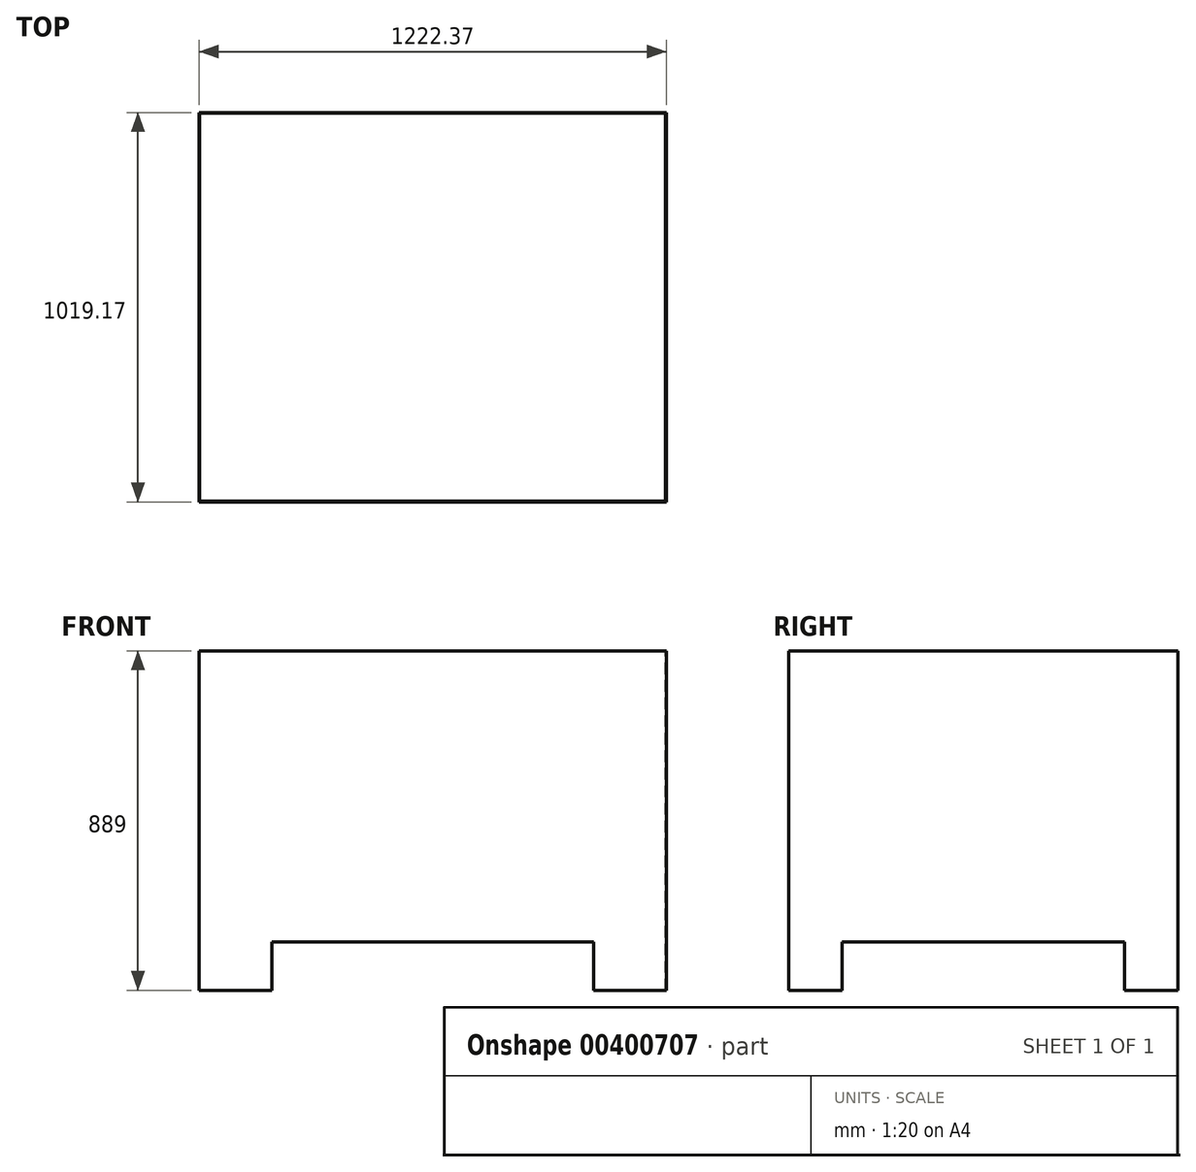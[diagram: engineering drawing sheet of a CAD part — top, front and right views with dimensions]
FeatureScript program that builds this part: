
annotation { "Feature Type Name" : "Feature", "Feature Type Description" : "" }
export const myFeature = defineFeature(function(context is Context, id is Id, definition is map)
    precondition{}
    {
        {
            var Q0;
            Q0=qCreatedBy(makeId("Front.planeOp"),FACE);
            var sketch = newSketch(context, id + "F0", { "sketchPlane" : qUnion([Q0])});
            skLineSegment(sketch, "E0.bottom", {"start": v(0, 0) * mm, "end": v(481.25, 0) * mm});
            skLineSegment(sketch, "E0.top", {"start": v(0, 350) * mm, "end": v(481.25, 350) * mm});
            skLineSegment(sketch, "E0.left", {"start": v(0, 0) * mm, "end": v(0, 350) * mm});
            skLineSegment(sketch, "E0.right", {"start": v(481.25, 0) * mm, "end": v(481.25, 350) * mm});
            skSolve(sketch);
        }
        {
            var Q0;
            Q0 = qSketchRegion(id + "F0", true);
            extrude(context, id + "F1", {"entities" : qUnion([Q0]), "oppositeDirection" : true, "depth" : 401.25 * mm});
        }
        {
            var Q0;
            Q0=makeQuery(id+"F1.opExtrude","SWEPT_FACE",FACE,{"disambiguationData":[OSD([sQuery(id+"F0.wireOp",EDGE,"E0.top")])]});
            var sketch = newSketch(context, id + "F2", { "sketchPlane" : qUnion([Q0])});
            skLineSegment(sketch, "E1.bottom", {"start": v(480.62, 0.63) * mm, "end": v(0.62, 0.63) * mm});
            skLineSegment(sketch, "E1.top", {"start": v(480.62, 400.63) * mm, "end": v(0.62, 400.63) * mm});
            skLineSegment(sketch, "E1.left", {"start": v(480.62, 0.63) * mm, "end": v(480.62, 400.63) * mm});
            skLineSegment(sketch, "E1.right", {"start": v(0.62, 0.63) * mm, "end": v(0.62, 400.63) * mm});
            skPoint(sketch, "E1.middle", {"position": v(240.62, 200.63) * mm});
            skPoint(sketch, "E1.middle.positionSnap0", {"position": v(0, 200.63) * mm});
            skPoint(sketch, "E1.middle.positionSnap1", {"position": v(240.62, 401.25) * mm});
            skPoint(sketch, "E1.centerSnap0", {"position": v(0, 200.63) * mm});
            skPoint(sketch, "E1.centerSnap1", {"position": v(240.62, 401.25) * mm});
            skSolve(sketch);
        }
        {
            var Q0;
            Q0 = qSketchRegion(id + "F2", true);
            extrude(context, id + "F3", {"entities" : qUnion([Q0]), "operationType" : NewBodyOperationType.REMOVE, "endBound" : BoundingType.THROUGH_ALL, "oppositeDirection" : true, "depth" : 25 * mm});
        }
        {
            var Q0;
            Q0=makeQuery(id+"F1.opExtrude","SWEPT_FACE",FACE,{"disambiguationData":[OSD([sQuery(id+"F0.wireOp",EDGE,"E0.left")])]});
            var sketch = newSketch(context, id + "F4", { "sketchPlane" : qUnion([Q0])});
            skLineSegment(sketch, "E2", {"start": v(-401.25, 0) * mm, "end": v(-346.25, 0) * mm});
            skLineSegment(sketch, "E3", {"start": v(-346.25, 0) * mm, "end": v(-346.25, 50) * mm});
            skLineSegment(sketch, "E4.bottom", {"start": v(-346.25, 50) * mm, "end": v(-55, 50) * mm});
            skLineSegment(sketch, "E4.top", {"start": v(-346.25, -50) * mm, "end": v(-55, -50) * mm});
            skLineSegment(sketch, "E4.left", {"start": v(-346.25, 50) * mm, "end": v(-346.25, -50) * mm});
            skLineSegment(sketch, "E4.right", {"start": v(-55, 50) * mm, "end": v(-55, -50) * mm});
            skPoint(sketch, "E4.middle", {"position": v(-200.63, 0) * mm});
            skSolve(sketch);
        }
        {
            var Q0;
            Q0 = qSketchRegion(id + "F4", true);
            extrude(context, id + "F5", {"entities" : qUnion([Q0]), "operationType" : NewBodyOperationType.REMOVE, "endBound" : BoundingType.THROUGH_ALL, "oppositeDirection" : true, "depth" : 25 * mm});
        }
        {
            var Q0;
            Q0=makeQuery(id+"F1.opExtrude","CAP_FACE",FACE,{"disambiguationData":[OSD([sQuery(id+"F0.wireOp",EDGE,"E0.bottom"),sQuery(id+"F0.wireOp",EDGE,"E0.top"),sQuery(id+"F0.wireOp",EDGE,"E0.left"),sQuery(id+"F0.wireOp",EDGE,"E0.right")])],"isStart":true});
            var sketch = newSketch(context, id + "F6", { "sketchPlane" : qUnion([Q0])});
            skLineSegment(sketch, "E5", {"start": v(0, 0) * mm, "end": v(75, 0) * mm});
            skLineSegment(sketch, "E6", {"start": v(75, 0) * mm, "end": v(75, 50) * mm});
            skLineSegment(sketch, "E7.bottom", {"start": v(75, 50) * mm, "end": v(406.25, 50) * mm});
            skLineSegment(sketch, "E7.top", {"start": v(75, -50) * mm, "end": v(406.25, -50) * mm});
            skLineSegment(sketch, "E7.left", {"start": v(75, 50) * mm, "end": v(75, -50) * mm});
            skLineSegment(sketch, "E7.right", {"start": v(406.25, 50) * mm, "end": v(406.25, -50) * mm});
            skPoint(sketch, "E7.middle", {"position": v(240.62, 0) * mm});
            skSolve(sketch);
        }
        {
            var Q0;
            Q0 = qSketchRegion(id + "F6", true);
            extrude(context, id + "F7", {"entities" : qUnion([Q0]), "operationType" : NewBodyOperationType.REMOVE, "endBound" : BoundingType.THROUGH_ALL, "oppositeDirection" : true, "depth" : 25 * mm});
        }
        {
            var Q0;
            Q0=makeQuery(id+"F1.opExtrude","SWEPT_BODY",BODY,{"disambiguationData":[OSD([sQuery(id+"F0.wireOp",EDGE,"E0.bottom"),sQuery(id+"F0.wireOp",EDGE,"E0.top"),sQuery(id+"F0.wireOp",EDGE,"E0.left"),sQuery(id+"F0.wireOp",EDGE,"E0.right")])]});
            var Q1;
            Q1=makeQuery(id+"F1.opExtrude","CAP_VERTEX",VERTEX,{"disambiguationData":[OSD([sQuery(id+"F0.wireOp",EDGE,"E0.bottom"),sQuery(id+"F0.wireOp",EDGE,"E0.right")])],"isStart":true});
            transform(context, id + "F8", {"entities" : qUnion([Q0]), "transformType" : TransformType.SCALE_UNIFORMLY, "scale" : 2.54, "scalePoint" : qUnion([Q1]), "makeCopy" : false});
        }
    });
